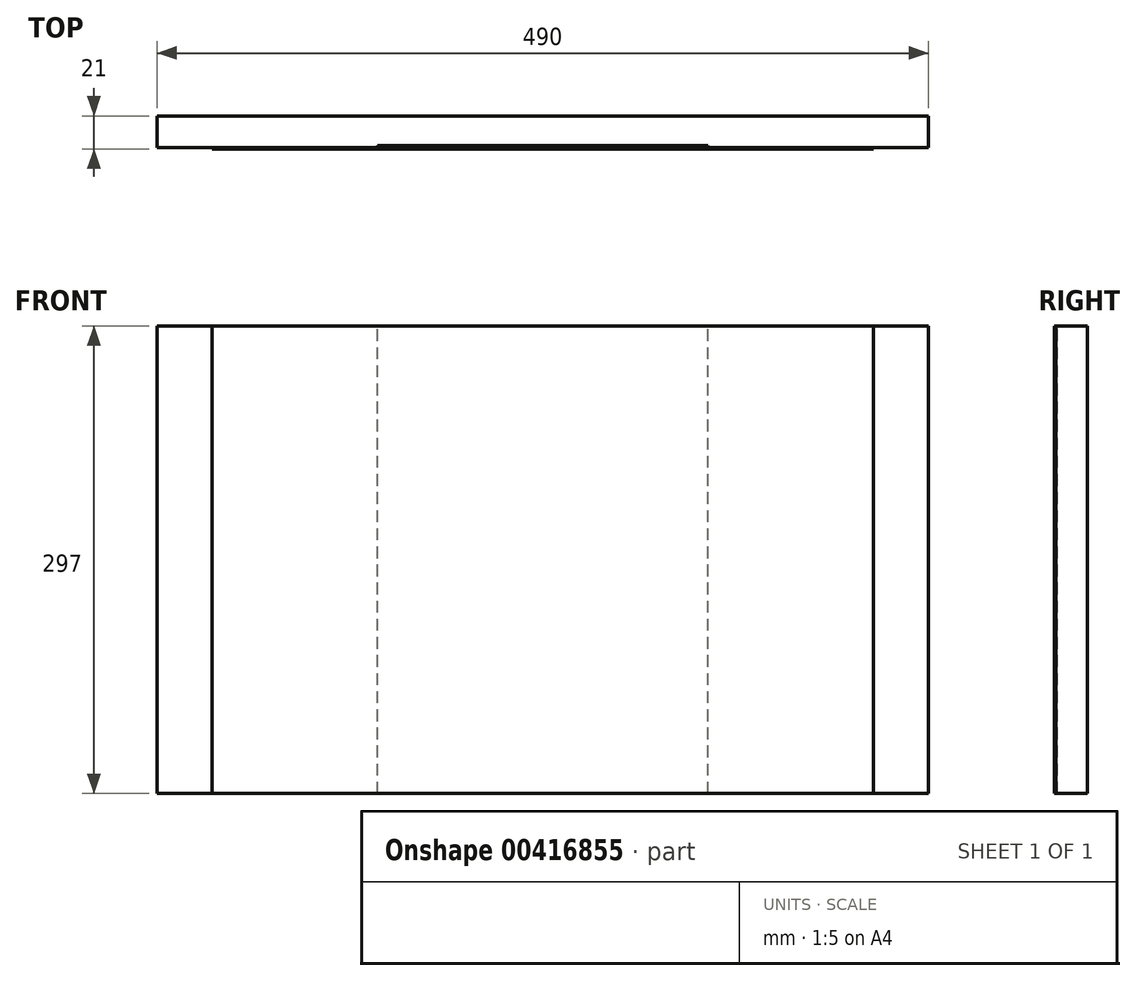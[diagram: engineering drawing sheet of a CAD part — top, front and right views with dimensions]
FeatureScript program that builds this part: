
annotation { "Feature Type Name" : "Feature", "Feature Type Description" : "" }
export const myFeature = defineFeature(function(context is Context, id is Id, definition is map)
    precondition{}
    {
        {
            var Q0;
            Q0=qCreatedBy(makeId("Front.planeOp"),FACE);
            var sketch = newSketch(context, id + "F0", { "sketchPlane" : qUnion([Q0])});
            skLineSegment(sketch, "E0.bottom", {"start": v(-245, 148.5) * mm, "end": v(245, 148.5) * mm});
            skLineSegment(sketch, "E0.top", {"start": v(-245, -148.5) * mm, "end": v(245, -148.5) * mm});
            skLineSegment(sketch, "E0.left", {"start": v(-245, 148.5) * mm, "end": v(-245, -148.5) * mm});
            skLineSegment(sketch, "E0.right", {"start": v(245, 148.5) * mm, "end": v(245, -148.5) * mm});
            skPoint(sketch, "E0.middle", {"position": v(0, 0) * mm});
            skSolve(sketch);
        }
        {
            var Q0;
            Q0 = qSketchRegion(id + "F0", true);
            extrude(context, id + "F1", {"entities" : qUnion([Q0]), "oppositeDirection" : true, "depth" : 20 * mm});
        }
        {
            var Q0;
            Q0=makeQuery(id+"F1.opExtrude","CAP_FACE",FACE,{"disambiguationData":[OSD([sQuery(id+"F0.wireOp",EDGE,"E0.bottom"),sQuery(id+"F0.wireOp",EDGE,"E0.top"),sQuery(id+"F0.wireOp",EDGE,"E0.left"),sQuery(id+"F0.wireOp",EDGE,"E0.right")])],"isStart":true});
            var sketch = newSketch(context, id + "F2", { "sketchPlane" : qUnion([Q0])});
            skLineSegment(sketch, "E1", {"start": v(0, 0) * mm, "end": v(0, 0) * mm});
            skLineSegment(sketch, "E2.bottom", {"start": v(-105, -148.5) * mm, "end": v(105, -148.5) * mm});
            skLineSegment(sketch, "E2.top", {"start": v(-105, 148.5) * mm, "end": v(105, 148.5) * mm});
            skLineSegment(sketch, "E2.left", {"start": v(-105, -148.5) * mm, "end": v(-105, 148.5) * mm});
            skLineSegment(sketch, "E2.right", {"start": v(105, -148.5) * mm, "end": v(105, 148.5) * mm});
            skPoint(sketch, "E2.middle", {"position": v(0, 0) * mm});
            skSolve(sketch);
        }
        {
            var Q0;
            Q0=makeQuery(id+"F2.imprint","IMPRINT",FACE,{"disambiguationData":[TD([[makeQuery(id+"F2.imprint","IMPRINT",EDGE,{"derivedFrom":makeQuery(id+"F1.opExtrude","CAP_EDGE",EDGE,{"disambiguationData":[OSD([sQuery(id+"F0.wireOp",EDGE,"E0.bottom")])],"isStart":true})}),-1.0]])]});
            var sketch = newSketch(context, id + "F3", { "sketchPlane" : qUnion([Q0])});
            skLineSegment(sketch, "E3", {"start": v(0, 0) * mm, "end": v(0, 0) * mm});
            skLineSegment(sketch, "E4.bottom", {"start": v(-210, 148.5) * mm, "end": v(210, 148.5) * mm});
            skLineSegment(sketch, "E4.top", {"start": v(-210, -148.5) * mm, "end": v(210, -148.5) * mm});
            skLineSegment(sketch, "E4.left", {"start": v(-210, 148.5) * mm, "end": v(-210, -148.5) * mm});
            skLineSegment(sketch, "E4.right", {"start": v(210, 148.5) * mm, "end": v(210, -148.5) * mm});
            skPoint(sketch, "E4.middle", {"position": v(0, 0) * mm});
            skSolve(sketch);
        }
        {
            var Q0;
            Q0=makeQuery(id+"F2.imprint","IMPRINT",FACE,{"disambiguationData":[TD([[makeQuery(id+"F2.imprint","IMPRINT",EDGE,{"derivedFrom":sQuery(id+"F2.wireOp",EDGE,"E2.bottom")}),1.0]])]});
            extrude(context, id + "F4", {"entities" : qUnion([Q0]), "oppositeDirection" : true, "depth" : 1 * mm});
        }
        {
            var Q0;
            Q0 = qSketchRegion(id + "F3", true);
            extrude(context, id + "F5", {"entities" : qUnion([Q0]), "depth" : 1 * mm});
        }
    });
